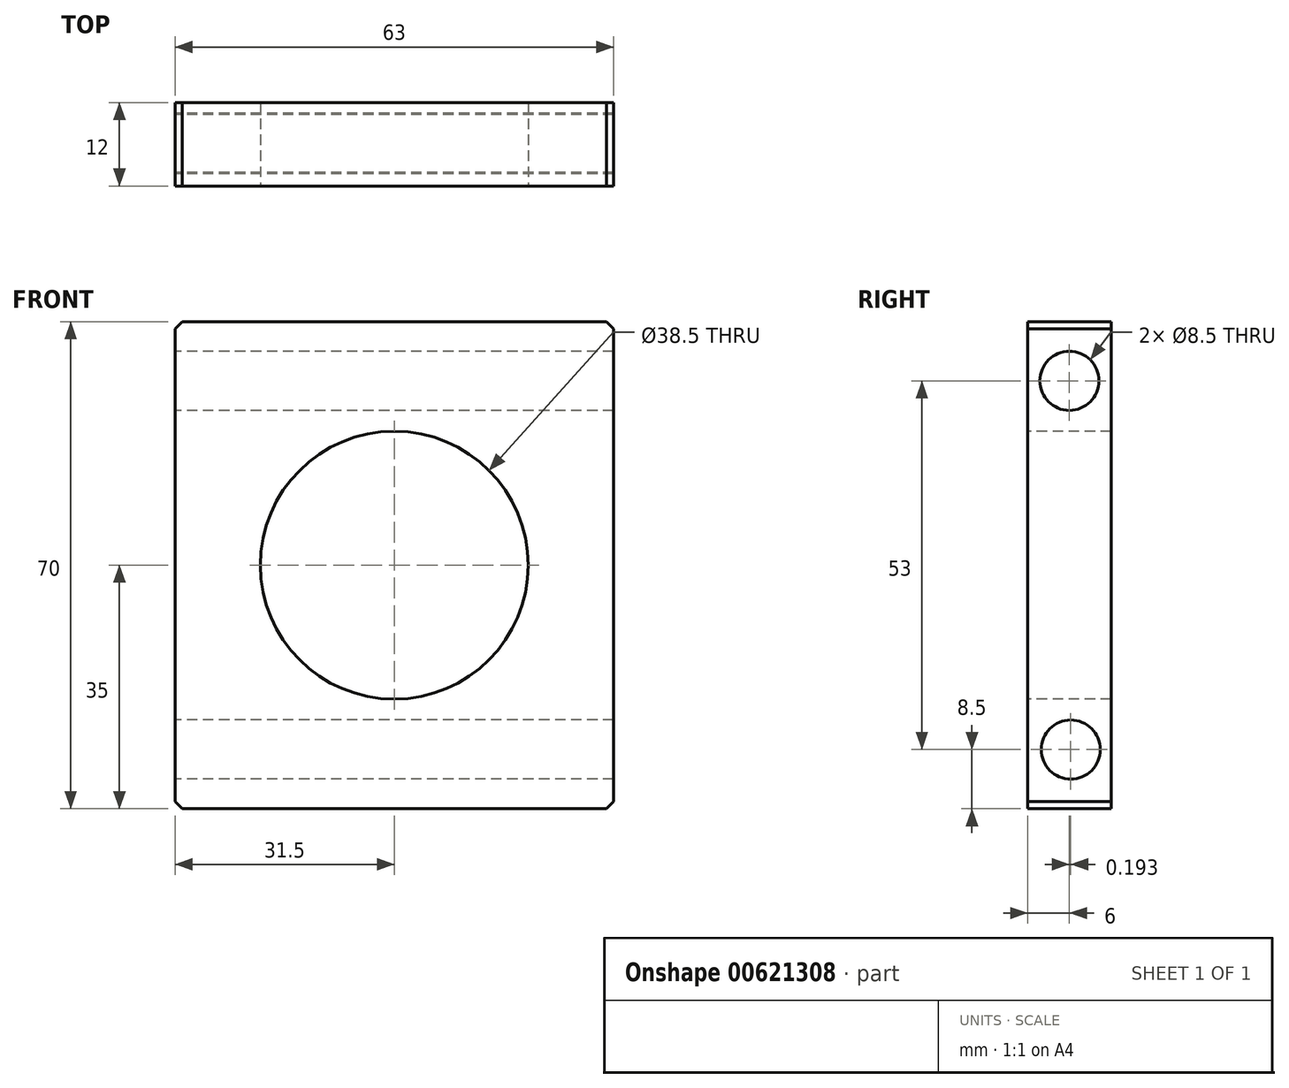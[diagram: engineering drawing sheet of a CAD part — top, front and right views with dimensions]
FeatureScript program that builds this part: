
annotation { "Feature Type Name" : "Feature", "Feature Type Description" : "" }
export const myFeature = defineFeature(function(context is Context, id is Id, definition is map)
    precondition{}
    {
        {
            var Q0;
            Q0=qCreatedBy(makeId("Front.planeOp"),FACE);
            var sketch = newSketch(context, id + "F0", { "sketchPlane" : qUnion([Q0])});
            skLineSegment(sketch, "E0.bottom", {"start": v(0, 0) * mm, "end": v(63, 0) * mm});
            skLineSegment(sketch, "E0.top", {"start": v(0, 70) * mm, "end": v(63, 70) * mm});
            skLineSegment(sketch, "E0.left", {"start": v(0, 0) * mm, "end": v(0, 70) * mm});
            skLineSegment(sketch, "E0.right", {"start": v(63, 0) * mm, "end": v(63, 70) * mm});
            skSolve(sketch);
        }
        {
            var Q0;
            Q0 = qSketchRegion(id + "F0", true);
            extrude(context, id + "F1", {"entities" : qUnion([Q0]), "depth" : 12 * mm, "offsetDistance" : 25 * mm});
        }
        {
            var Q0;
            Q0=makeQuery(id+"F1.opExtrude","CAP_FACE",FACE,{"disambiguationData":[OSD([sQuery(id+"F0.wireOp",EDGE,"E0.bottom"),sQuery(id+"F0.wireOp",EDGE,"E0.top"),sQuery(id+"F0.wireOp",EDGE,"E0.left"),sQuery(id+"F0.wireOp",EDGE,"E0.right")])],"isStart":false});
            var sketch = newSketch(context, id + "F2", { "sketchPlane" : qUnion([Q0])});
            skCircle(sketch, "E1", {"center": v(31.5, 35) * mm, "radius": 19.25 * mm});
            skPoint(sketch, "E1.centerSnap0", {"position": v(0, 35) * mm});
            skPoint(sketch, "E1.centerSnap1", {"position": v(31.5, 0) * mm});
            skSolve(sketch);
        }
        {
            var Q0;
            Q0 = qSketchRegion(id + "F2", true);
            extrude(context, id + "F3", {"entities" : qUnion([Q0]), "operationType" : NewBodyOperationType.REMOVE, "oppositeDirection" : true, "depth" : 25 * mm, "offsetDistance" : 25 * mm});
        }
        {
            var Q0;
            Q0=makeQuery(id+"F1.opExtrude","SWEPT_FACE",FACE,{"disambiguationData":[OSD([sQuery(id+"F0.wireOp",EDGE,"E0.left")])]});
            var sketch = newSketch(context, id + "F4", { "sketchPlane" : qUnion([Q0])});
            skCircle(sketch, "E2", {"center": v(6, 61.5) * mm, "radius": 4.25 * mm});
            skCircle(sketch, "E3.1.0.0", {"center": v(5.8, 8.5) * mm, "radius": 4.25 * mm});
            skLineSegment(sketch, "E3.direction1", {"start": v(6, 61.5) * mm, "end": v(5.8, 8.5) * mm, "construction": true});
            skSolve(sketch);
        }
        {
            var Q0;
            Q0 = qSketchRegion(id + "F4", true);
            extrude(context, id + "F5", {"entities" : qUnion([Q0]), "operationType" : NewBodyOperationType.REMOVE, "endBound" : BoundingType.THROUGH_ALL, "oppositeDirection" : true, "depth" : 25 * mm, "offsetDistance" : 25 * mm});
        }
        {
            var Q0;
            Q0=makeQuery(id+"F1.opExtrude","SWEPT_EDGE",EDGE,{"disambiguationData":[OSD([sQuery(id+"F0.wireOp",EDGE,"E0.top"),sQuery(id+"F0.wireOp",EDGE,"E0.right")])]});
            var Q1;
            Q1=makeQuery(id+"F1.opExtrude","SWEPT_EDGE",EDGE,{"disambiguationData":[OSD([sQuery(id+"F0.wireOp",EDGE,"E0.bottom"),sQuery(id+"F0.wireOp",EDGE,"E0.right")])]});
            var Q2;
            Q2=makeQuery(id+"F1.opExtrude","SWEPT_EDGE",EDGE,{"disambiguationData":[OSD([sQuery(id+"F0.wireOp",EDGE,"E0.bottom"),sQuery(id+"F0.wireOp",EDGE,"E0.left")])]});
            var Q3;
            Q3=makeQuery(id+"F1.opExtrude","SWEPT_EDGE",EDGE,{"disambiguationData":[OSD([sQuery(id+"F0.wireOp",EDGE,"E0.top"),sQuery(id+"F0.wireOp",EDGE,"E0.left")])]});
            chamfer(context, id + "F6", {"entities" : qUnion([Q0, Q1, Q2, Q3]), "width" : 1 * mm, "tangentPropagation" : true});
        }
    });
